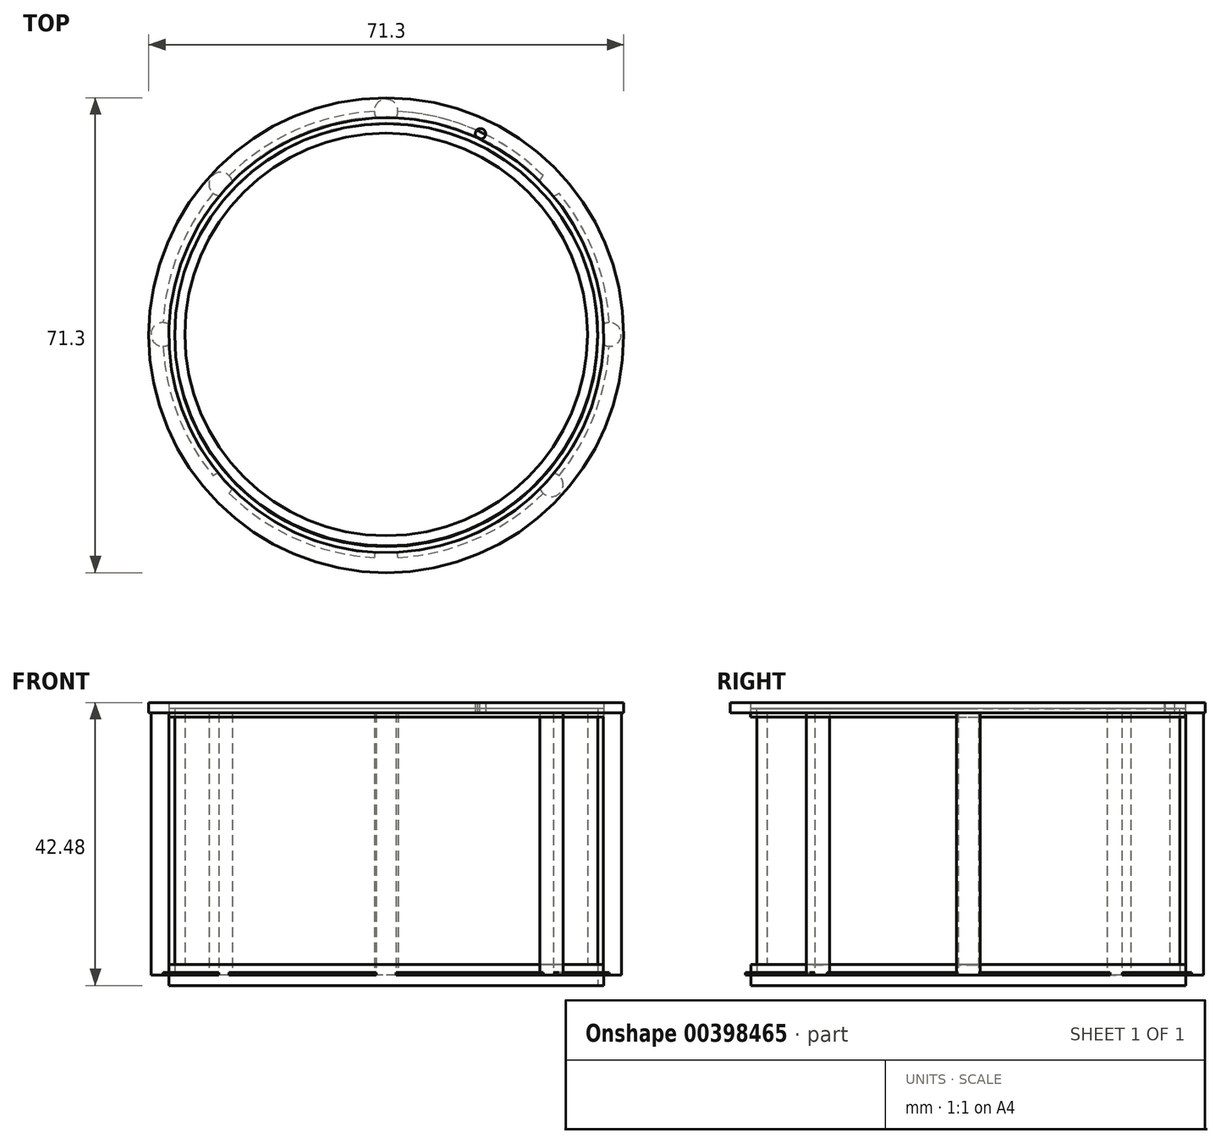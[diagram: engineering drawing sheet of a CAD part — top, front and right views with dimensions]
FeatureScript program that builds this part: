
annotation { "Feature Type Name" : "Feature", "Feature Type Description" : "" }
export const myFeature = defineFeature(function(context is Context, id is Id, definition is map)
    precondition{}
    {
        {
            var Q0;
            Q0=qCreatedBy(makeId("Top.planeOp"),FACE);
            var sketch = newSketch(context, id + "F0", { "sketchPlane" : qUnion([Q0])});
            skCircle(sketch, "E0", {"center": v(0, 0) * mm, "radius": 31.75 * mm});
            skCircle(sketch, "E1.0", {"center": v(0, 0) * mm, "radius": 32.64 * mm});
            skArc(sketch, "E2.0", {"start": v(-1.78, 33.48) * mm, "mid": v(-13.56, 30.67) * mm, "end": v(-23.57, 23.85) * mm});
            skArc(sketch, "E3.trimOffspring", {"start": v(1.78, 33.48) * mm, "mid": v(0, 35.3) * mm, "end": v(-1.78, 33.48) * mm});
            skArc(sketch, "E4.trimOffspring", {"start": v(1.78, -33.48) * mm, "mid": v(13.56, -30.67) * mm, "end": v(23.57, -23.85) * mm});
            skArc(sketch, "E5.trimOffspring", {"start": v(1.78, -33.48) * mm, "mid": v(0, -35.3) * mm, "end": v(-1.78, -33.48) * mm});
            skArc(sketch, "E6", {"start": v(-33.48, 1.78) * mm, "mid": v(-35.3, 0) * mm, "end": v(-33.48, -1.78) * mm});
            skArc(sketch, "E7", {"start": v(33.48, -1.78) * mm, "mid": v(35.3, 0) * mm, "end": v(33.48, 1.78) * mm});
            skArc(sketch, "E8.MirrorC", {"start": v(-23.57, -23.85) * mm, "mid": v(-26.11, -23.76) * mm, "end": v(-25.96, -21.22) * mm});
            skArc(sketch, "E9.MirrorC", {"start": v(23.57, -23.85) * mm, "mid": v(26.11, -23.76) * mm, "end": v(25.96, -21.22) * mm});
            skArc(sketch, "E10.MirrorC", {"start": v(23.57, 23.85) * mm, "mid": v(26.11, 23.76) * mm, "end": v(25.96, 21.22) * mm});
            skLineSegment(sketch, "E11", {"start": v(12.03, 31.3) * mm, "end": v(12.79, 33.23) * mm});
            skLineSegment(sketch, "E12", {"start": v(12.79, 33.23) * mm, "end": v(14.96, 32.39) * mm});
            skLineSegment(sketch, "E13", {"start": v(14.96, 32.39) * mm, "end": v(14.18, 30.38) * mm});
            skCircle(sketch, "E14", {"center": v(13.5, 31.8) * mm, "radius": 0.78 * mm});
            skPoint(sketch, "E14.first.point", {"position": v(13.63, 32.56) * mm});
            skPoint(sketch, "E14.second.point", {"position": v(13.3, 31.04) * mm});
            skPoint(sketch, "E14.third.point", {"position": v(13.64, 31.03) * mm});
            skArc(sketch, "E15.trimOffspring", {"start": v(25.96, -21.22) * mm, "mid": v(31.27, -12.1) * mm, "end": v(33.48, -1.78) * mm});
            skArc(sketch, "E16.trimOffspring", {"start": v(-23.57, -23.85) * mm, "mid": v(-13.56, -30.67) * mm, "end": v(-1.78, -33.48) * mm});
            skArc(sketch, "E17.trimOffspring", {"start": v(-33.48, -1.78) * mm, "mid": v(-31.27, -12.1) * mm, "end": v(-25.96, -21.22) * mm});
            skArc(sketch, "E18.trimOffspring", {"start": v(33.48, 1.78) * mm, "mid": v(31.27, 12.1) * mm, "end": v(25.96, 21.22) * mm});
            skArc(sketch, "E19.trimOffspring", {"start": v(23.57, 23.85) * mm, "mid": v(13.56, 30.67) * mm, "end": v(1.78, 33.48) * mm});
            skArc(sketch, "E20.trimOffspring", {"start": v(-25.96, 21.22) * mm, "mid": v(-31.27, 12.1) * mm, "end": v(-33.48, 1.78) * mm});
            skArc(sketch, "E21", {"start": v(25.96, -21.22) * mm, "mid": v(23.48, -21.37) * mm, "end": v(23.57, -23.85) * mm});
            skArc(sketch, "E22", {"start": v(33.48, 1.78) * mm, "mid": v(31.75, 0) * mm, "end": v(33.48, -1.78) * mm});
            skArc(sketch, "E23", {"start": v(1.78, 33.48) * mm, "mid": v(0, 31.75) * mm, "end": v(-1.78, 33.48) * mm});
            skArc(sketch, "E24", {"start": v(23.57, 23.85) * mm, "mid": v(23.48, 21.37) * mm, "end": v(25.96, 21.22) * mm});
            skArc(sketch, "E25", {"start": v(-33.48, 1.78) * mm, "mid": v(-31.75, 0) * mm, "end": v(-33.48, -1.78) * mm});
            skArc(sketch, "E26", {"start": v(-25.96, -21.22) * mm, "mid": v(-23.48, -21.37) * mm, "end": v(-23.57, -23.85) * mm});
            skArc(sketch, "E27", {"start": v(1.78, -33.48) * mm, "mid": v(0, -31.75) * mm, "end": v(-1.78, -33.48) * mm});
            skCircle(sketch, "E28", {"center": v(-24.82, 22.59) * mm, "radius": 1.78 * mm});
            skPoint(sketch, "E28.third.point", {"position": v(-26.55, 22.18) * mm});
            skSolve(sketch);
        }
        {
            var Q0;
            Q0=makeQuery(id+"F0.imprint","IMPRINT",FACE,{"disambiguationData":[TD([[makeQuery(id+"F0.imprint","IMPRINT",EDGE,{"derivedFrom":sQuery(id+"F0.wireOp",EDGE,"E0")}),1.0]])]});
            var Q1;
            {var subQ4=sQuery(id+"F0.wireOp",EDGE,"E7");Q1=makeQuery(id+"F0.imprint","IMPRINT",FACE,{"disambiguationData":[TD([[makeQuery(id+"F0.imprint","IMPRINT",EDGE,{"derivedFrom":subQ4}),1.0]])]});}
            var Q2;
            {var subQ4=sQuery(id+"F0.wireOp",EDGE,"E9.MirrorC");Q2=makeQuery(id+"F0.imprint","IMPRINT",FACE,{"disambiguationData":[TD([[makeQuery(id+"F0.imprint","IMPRINT",EDGE,{"derivedFrom":subQ4}),1.0]])]});}
            var Q3;
            Q3=makeQuery(id+"F0.imprint","IMPRINT",FACE,{"disambiguationData":[TD([[makeQuery(id+"F0.imprint","IMPRINT",EDGE,{"derivedFrom":sQuery(id+"F0.wireOp",EDGE,"E5.trimOffspring")}),-1.0]])]});
            var Q4;
            Q4=makeQuery(id+"F0.imprint","IMPRINT",FACE,{"disambiguationData":[TD([[makeQuery(id+"F0.imprint","IMPRINT",EDGE,{"derivedFrom":sQuery(id+"F0.wireOp",EDGE,"E8.MirrorC")}),-1.0]])]});
            var Q5;
            Q5=makeQuery(id+"F0.imprint","IMPRINT",FACE,{"disambiguationData":[TD([[makeQuery(id+"F0.imprint","IMPRINT",EDGE,{"derivedFrom":sQuery(id+"F0.wireOp",EDGE,"E10.MirrorC")}),-1.0]])]});
            var Q6;
            Q6=makeQuery(id+"F0.imprint","IMPRINT",FACE,{"disambiguationData":[TD([[makeQuery(id+"F0.imprint","IMPRINT",EDGE,{"derivedFrom":sQuery(id+"F0.wireOp",EDGE,"E3.trimOffspring")}),1.0]])]});
            var Q7;
            Q7=makeQuery(id+"F0.imprint","IMPRINT",FACE,{"disambiguationData":[TD([[makeQuery(id+"F0.imprint","IMPRINT",EDGE,{"derivedFrom":sQuery(id+"F0.wireOp",EDGE,"882b732f-c852-48f1-b691-361df414e5d00.MirrorC")}),1.0]])]});
            var Q8;
            {var subQ0=sQuery(id+"F0.wireOp",EDGE,"E28");var subQ1=sQuery(id+"F0.wireOp",EDGE,"E1.0");var subQ2=makeQuery(id+"F0.imprint","INTERSECT",VERTEX,{"disambiguationData":[OD(0.0)],"derivedFrom":[subQ1,subQ0]});Q8=makeQuery(id+"F0.imprint","IMPRINT",FACE,{"disambiguationData":[TD([[makeQuery(id+"F0.imprint","IMPRINT",EDGE,{"disambiguationData":[TD([[subQ2,-1.0]])],"derivedFrom":subQ1}),-1.0]])]});}
            var Q9;
            {var subQ4=sQuery(id+"F0.wireOp",EDGE,"E6");Q9=makeQuery(id+"F0.imprint","IMPRINT",FACE,{"disambiguationData":[TD([[makeQuery(id+"F0.imprint","IMPRINT",EDGE,{"derivedFrom":subQ4}),1.0]])]});}
            extrude(context, id + "F1", {"entities" : qUnion([Q0, Q1, Q2, Q3, Q4, Q5, Q6, Q7, Q8, Q9]), "depth" : 39.37 * mm});
        }
        {
            var Q0;
            {var subQ0=sQuery(id+"F0.wireOp",EDGE,"E23");var subQ1=sQuery(id+"F0.wireOp",EDGE,"E0");var subQ2=makeQuery(id+"F0.imprint","INTERSECT",VERTEX,{"derivedFrom":[subQ1,subQ0]});Q0=makeQuery(id+"F0.imprint","IMPRINT",FACE,{"disambiguationData":[TD([[makeQuery(id+"F0.imprint","IMPRINT",EDGE,{"disambiguationData":[TD([[subQ2,-1.0]])],"derivedFrom":subQ1}),-1.0]])]});}
            var Q1;
            {var subQ0=sQuery(id+"F0.wireOp",EDGE,"E28");var subQ1=sQuery(id+"F0.wireOp",EDGE,"E1.0");var subQ2=makeQuery(id+"F0.imprint","INTERSECT",VERTEX,{"disambiguationData":[OD(0.0)],"derivedFrom":[subQ1,subQ0]});Q1=makeQuery(id+"F0.imprint","IMPRINT",FACE,{"disambiguationData":[TD([[makeQuery(id+"F0.imprint","IMPRINT",EDGE,{"disambiguationData":[TD([[subQ2,-1.0]])],"derivedFrom":subQ1}),1.0]])]});}
            var Q2;
            {var subQ0=sQuery(id+"F0.wireOp",EDGE,"E24");var subQ1=sQuery(id+"F0.wireOp",EDGE,"E0");var subQ2=makeQuery(id+"F0.imprint","INTERSECT",VERTEX,{"derivedFrom":[subQ1,subQ0]});Q2=makeQuery(id+"F0.imprint","IMPRINT",FACE,{"disambiguationData":[TD([[makeQuery(id+"F0.imprint","IMPRINT",EDGE,{"disambiguationData":[TD([[subQ2,-1.0]])],"derivedFrom":subQ1}),-1.0]])]});}
            var Q3;
            {var subQ0=sQuery(id+"F0.wireOp",EDGE,"E23");var subQ1=sQuery(id+"F0.wireOp",EDGE,"E1.0");var subQ2=makeQuery(id+"F0.imprint","INTERSECT",VERTEX,{"disambiguationData":[OD(0.0)],"derivedFrom":[subQ1,subQ0]});Q3=makeQuery(id+"F0.imprint","IMPRINT",FACE,{"disambiguationData":[TD([[makeQuery(id+"F0.imprint","IMPRINT",EDGE,{"disambiguationData":[TD([[subQ2,-1.0]])],"derivedFrom":subQ1}),1.0]])]});}
            var Q4;
            {var subQ0=sQuery(id+"F0.wireOp",EDGE,"E24");var subQ1=sQuery(id+"F0.wireOp",EDGE,"E1.0");var subQ2=makeQuery(id+"F0.imprint","INTERSECT",VERTEX,{"disambiguationData":[OD(0.0)],"derivedFrom":[subQ1,subQ0]});Q4=makeQuery(id+"F0.imprint","IMPRINT",FACE,{"disambiguationData":[TD([[makeQuery(id+"F0.imprint","IMPRINT",EDGE,{"disambiguationData":[TD([[subQ2,-1.0]])],"derivedFrom":subQ1}),1.0]])]});}
            var Q5;
            {var subQ0=sQuery(id+"F0.wireOp",EDGE,"E24");var subQ1=sQuery(id+"F0.wireOp",EDGE,"E0");var subQ2=makeQuery(id+"F0.imprint","INTERSECT",VERTEX,{"derivedFrom":[subQ1,subQ0]});Q5=makeQuery(id+"F0.imprint","IMPRINT",FACE,{"disambiguationData":[TD([[makeQuery(id+"F0.imprint","IMPRINT",EDGE,{"disambiguationData":[TD([[subQ2,1.0]])],"derivedFrom":subQ1}),-1.0]])]});}
            var Q6;
            {var subQ0=sQuery(id+"F0.wireOp",EDGE,"E22");var subQ1=sQuery(id+"F0.wireOp",EDGE,"E1.0");var subQ2=makeQuery(id+"F0.imprint","INTERSECT",VERTEX,{"disambiguationData":[OD(0.0)],"derivedFrom":[subQ1,subQ0]});Q6=makeQuery(id+"F0.imprint","IMPRINT",FACE,{"disambiguationData":[TD([[makeQuery(id+"F0.imprint","IMPRINT",EDGE,{"disambiguationData":[TD([[subQ2,1.0]])],"derivedFrom":subQ1}),1.0]])]});}
            var Q7;
            {var subQ0=sQuery(id+"F0.wireOp",EDGE,"E22");var subQ1=sQuery(id+"F0.wireOp",EDGE,"E0");var subQ2=makeQuery(id+"F0.imprint","INTERSECT",VERTEX,{"derivedFrom":[subQ1,subQ0]});Q7=makeQuery(id+"F0.imprint","IMPRINT",FACE,{"disambiguationData":[TD([[makeQuery(id+"F0.imprint","IMPRINT",EDGE,{"disambiguationData":[TD([[subQ2,1.0]])],"derivedFrom":subQ1}),-1.0]])]});}
            var Q8;
            {var subQ0=sQuery(id+"F0.wireOp",EDGE,"E21");var subQ1=sQuery(id+"F0.wireOp",EDGE,"E1.0");var subQ2=makeQuery(id+"F0.imprint","INTERSECT",VERTEX,{"disambiguationData":[OD(0.0)],"derivedFrom":[subQ1,subQ0]});Q8=makeQuery(id+"F0.imprint","IMPRINT",FACE,{"disambiguationData":[TD([[makeQuery(id+"F0.imprint","IMPRINT",EDGE,{"disambiguationData":[TD([[subQ2,-1.0]])],"derivedFrom":subQ1}),1.0]])]});}
            var Q9;
            {var subQ0=sQuery(id+"F0.wireOp",EDGE,"E27");var subQ1=sQuery(id+"F0.wireOp",EDGE,"E0");var subQ2=makeQuery(id+"F0.imprint","INTERSECT",VERTEX,{"derivedFrom":[subQ1,subQ0]});Q9=makeQuery(id+"F0.imprint","IMPRINT",FACE,{"disambiguationData":[TD([[makeQuery(id+"F0.imprint","IMPRINT",EDGE,{"disambiguationData":[TD([[subQ2,-1.0]])],"derivedFrom":subQ1}),-1.0]])]});}
            var Q10;
            {var subQ0=sQuery(id+"F0.wireOp",EDGE,"E27");var subQ1=sQuery(id+"F0.wireOp",EDGE,"E1.0");var subQ2=makeQuery(id+"F0.imprint","INTERSECT",VERTEX,{"disambiguationData":[OD(0.0)],"derivedFrom":[subQ1,subQ0]});Q10=makeQuery(id+"F0.imprint","IMPRINT",FACE,{"disambiguationData":[TD([[makeQuery(id+"F0.imprint","IMPRINT",EDGE,{"disambiguationData":[TD([[subQ2,-1.0]])],"derivedFrom":subQ1}),1.0]])]});}
            var Q11;
            {var subQ0=sQuery(id+"F0.wireOp",EDGE,"E26");var subQ1=sQuery(id+"F0.wireOp",EDGE,"E0");var subQ2=makeQuery(id+"F0.imprint","INTERSECT",VERTEX,{"derivedFrom":[subQ1,subQ0]});Q11=makeQuery(id+"F0.imprint","IMPRINT",FACE,{"disambiguationData":[TD([[makeQuery(id+"F0.imprint","IMPRINT",EDGE,{"disambiguationData":[TD([[subQ2,-1.0]])],"derivedFrom":subQ1}),-1.0]])]});}
            var Q12;
            {var subQ0=sQuery(id+"F0.wireOp",EDGE,"E26");var subQ1=sQuery(id+"F0.wireOp",EDGE,"E1.0");var subQ2=makeQuery(id+"F0.imprint","INTERSECT",VERTEX,{"disambiguationData":[OD(0.0)],"derivedFrom":[subQ1,subQ0]});Q12=makeQuery(id+"F0.imprint","IMPRINT",FACE,{"disambiguationData":[TD([[makeQuery(id+"F0.imprint","IMPRINT",EDGE,{"disambiguationData":[TD([[subQ2,-1.0]])],"derivedFrom":subQ1}),1.0]])]});}
            var Q13;
            {var subQ0=sQuery(id+"F0.wireOp",EDGE,"E25");var subQ1=sQuery(id+"F0.wireOp",EDGE,"E0");var subQ2=makeQuery(id+"F0.imprint","INTERSECT",VERTEX,{"derivedFrom":[subQ1,subQ0]});Q13=makeQuery(id+"F0.imprint","IMPRINT",FACE,{"disambiguationData":[TD([[makeQuery(id+"F0.imprint","IMPRINT",EDGE,{"disambiguationData":[TD([[subQ2,-1.0]])],"derivedFrom":subQ1}),-1.0]])]});}
            var Q14;
            {var subQ0=sQuery(id+"F0.wireOp",EDGE,"E25");var subQ1=sQuery(id+"F0.wireOp",EDGE,"E1.0");var subQ2=makeQuery(id+"F0.imprint","INTERSECT",VERTEX,{"disambiguationData":[OD(0.0)],"derivedFrom":[subQ1,subQ0]});Q14=makeQuery(id+"F0.imprint","IMPRINT",FACE,{"disambiguationData":[TD([[makeQuery(id+"F0.imprint","IMPRINT",EDGE,{"disambiguationData":[TD([[subQ2,-1.0]])],"derivedFrom":subQ1}),1.0]])]});}
            extrude(context, id + "F2", {"entities" : qUnion([Q0, Q1, Q2, Q3, Q4, Q5, Q6, Q7, Q8, Q9, Q10, Q11, Q12, Q13, Q14]), "endBound" : BoundingType.SYMMETRIC, "depth" : 3.17 * mm});
        }
        {
            var Q0;
            {var subQ5=sQuery(id+"F0.wireOp",EDGE,"E2.0");Q0=makeQuery(id+"F0.imprint","IMPRINT",FACE,{"disambiguationData":[TD([[makeQuery(id+"F0.imprint","IMPRINT",EDGE,{"derivedFrom":subQ5}),1.0]])]});}
            var Q1;
            {var subQ4=sQuery(id+"F0.wireOp",EDGE,"E24");var subQ5=sQuery(id+"F0.wireOp",EDGE,"E1.0");var subQ6=makeQuery(id+"F0.imprint","INTERSECT",VERTEX,{"disambiguationData":[OD(1.0)],"derivedFrom":[subQ5,subQ4]});Q1=makeQuery(id+"F0.imprint","IMPRINT",FACE,{"disambiguationData":[TD([[makeQuery(id+"F0.imprint","IMPRINT",EDGE,{"disambiguationData":[TD([[subQ6,-1.0]])],"derivedFrom":subQ5}),-1.0]])]});}
            var Q2;
            {var subQ5=sQuery(id+"F0.wireOp",EDGE,"E18.trimOffspring");Q2=makeQuery(id+"F0.imprint","IMPRINT",FACE,{"disambiguationData":[TD([[makeQuery(id+"F0.imprint","IMPRINT",EDGE,{"derivedFrom":subQ5}),1.0]])]});}
            var Q3;
            {var subQ5=sQuery(id+"F0.wireOp",EDGE,"E15.trimOffspring");Q3=makeQuery(id+"F0.imprint","IMPRINT",FACE,{"disambiguationData":[TD([[makeQuery(id+"F0.imprint","IMPRINT",EDGE,{"derivedFrom":subQ5}),1.0]])]});}
            var Q4;
            {var subQ5=sQuery(id+"F0.wireOp",EDGE,"E4.trimOffspring");Q4=makeQuery(id+"F0.imprint","IMPRINT",FACE,{"disambiguationData":[TD([[makeQuery(id+"F0.imprint","IMPRINT",EDGE,{"derivedFrom":subQ5}),1.0]])]});}
            var Q5;
            {var subQ5=sQuery(id+"F0.wireOp",EDGE,"E16.trimOffspring");Q5=makeQuery(id+"F0.imprint","IMPRINT",FACE,{"disambiguationData":[TD([[makeQuery(id+"F0.imprint","IMPRINT",EDGE,{"derivedFrom":subQ5}),1.0]])]});}
            var Q6;
            {var subQ5=sQuery(id+"F0.wireOp",EDGE,"E17.trimOffspring");Q6=makeQuery(id+"F0.imprint","IMPRINT",FACE,{"disambiguationData":[TD([[makeQuery(id+"F0.imprint","IMPRINT",EDGE,{"derivedFrom":subQ5}),1.0]])]});}
            var Q7;
            {var subQ5=sQuery(id+"F0.wireOp",EDGE,"E20.trimOffspring");Q7=makeQuery(id+"F0.imprint","IMPRINT",FACE,{"disambiguationData":[TD([[makeQuery(id+"F0.imprint","IMPRINT",EDGE,{"derivedFrom":subQ5}),1.0]])]});}
            extrude(context, id + "F3", {"entities" : qUnion([Q0, Q1, Q2, Q3, Q4, Q5, Q6, Q7]), "depth" : 0.38 * mm});
        }
        {
            var Q0;
            Q0=makeQuery(id+"F1.opExtrude","CAP_FACE",FACE,{"disambiguationData":[OSD([sQuery(id+"F0.wireOp",EDGE,"E0")])],"isStart":false});
            var sketch = newSketch(context, id + "F4", { "sketchPlane" : qUnion([Q0])});
            skCircle(sketch, "E29", {"center": v(0.02, -0.11) * mm, "radius": 31.75 * mm});
            skCircle(sketch, "E30.0", {"center": v(0.02, -0.11) * mm, "radius": 32.64 * mm});
            skPoint(sketch, "E31.center.orphan", {"position": v(0.7, 33.4) * mm});
            skLineSegment(sketch, "E32", {"start": v(13.14, 30.74) * mm, "end": v(13.46, 31.58) * mm});
            skLineSegment(sketch, "E33", {"start": v(13.46, 31.58) * mm, "end": v(15.63, 30.73) * mm});
            skLineSegment(sketch, "E34", {"start": v(15.63, 30.73) * mm, "end": v(15.25, 29.76) * mm});
            skCircle(sketch, "E35", {"center": v(14.17, 30.14) * mm, "radius": 0.78 * mm});
            skPoint(sketch, "E35.first.point", {"position": v(14.3, 30.9) * mm});
            skPoint(sketch, "E35.second.point", {"position": v(13.97, 29.39) * mm});
            skPoint(sketch, "E35.third.point", {"position": v(14.31, 29.37) * mm});
            skPoint(sketch, "E36.third.point", {"position": v(-25.88, 20.53) * mm});
            skCircle(sketch, "E37.0", {"center": v(0.02, -0.11) * mm, "radius": 35.65 * mm});
            skSolve(sketch);
        }
        {
            var Q0;
            {var subQ0=sQuery(id+"F4.wireOp",EDGE,"05f0027a-2171-4007-9836-8562fc80002a");var subQ1=sQuery(id+"F4.wireOp",EDGE,"E29");var subQ2=makeQuery(id+"F4.imprint","INTERSECT",VERTEX,{"disambiguationData":[OD(0.0)],"derivedFrom":[subQ1,subQ0]});Q0=makeQuery(id+"F4.imprint","IMPRINT",FACE,{"disambiguationData":[TD([[makeQuery(id+"F4.imprint","IMPRINT",EDGE,{"disambiguationData":[TD([[subQ2,-1.0]])],"derivedFrom":subQ1}),-1.0]])]});}
            var Q1;
            {var subQ0=sQuery(id+"F4.wireOp",EDGE,"05f0027a-2171-4007-9836-8562fc80002a");var subQ1=sQuery(id+"F4.wireOp",EDGE,"E29");var subQ2=makeQuery(id+"F4.imprint","INTERSECT",VERTEX,{"disambiguationData":[OD(1.0)],"derivedFrom":[subQ1,subQ0]});Q1=makeQuery(id+"F4.imprint","IMPRINT",FACE,{"disambiguationData":[TD([[makeQuery(id+"F4.imprint","IMPRINT",EDGE,{"disambiguationData":[TD([[subQ2,-1.0]])],"derivedFrom":subQ1}),-1.0]])]});}
            var Q2;
            {var subQ0=sQuery(id+"F4.wireOp",EDGE,"f87926d4-d22f-4db6-bb2e-eca88a423e5e");var subQ1=sQuery(id+"F4.wireOp",EDGE,"E29");var subQ2=makeQuery(id+"F4.imprint","INTERSECT",VERTEX,{"disambiguationData":[OD(1.0)],"derivedFrom":[subQ1,subQ0]});Q2=makeQuery(id+"F4.imprint","IMPRINT",FACE,{"disambiguationData":[TD([[makeQuery(id+"F4.imprint","IMPRINT",EDGE,{"disambiguationData":[TD([[subQ2,-1.0]])],"derivedFrom":subQ1}),-1.0]])]});}
            var Q3;
            {var subQ0=sQuery(id+"F4.wireOp",EDGE,"f87926d4-d22f-4db6-bb2e-eca88a423e5e");var subQ1=sQuery(id+"F4.wireOp",EDGE,"E29");var subQ2=makeQuery(id+"F4.imprint","INTERSECT",VERTEX,{"disambiguationData":[OD(0.0)],"derivedFrom":[subQ1,subQ0]});Q3=makeQuery(id+"F4.imprint","IMPRINT",FACE,{"disambiguationData":[TD([[makeQuery(id+"F4.imprint","IMPRINT",EDGE,{"disambiguationData":[TD([[subQ2,-1.0]])],"derivedFrom":subQ1}),-1.0]])]});}
            var Q4;
            {var subQ0=sQuery(id+"F4.wireOp",EDGE,"77c8a3e9-4459-4353-a445-deef52aa50ce");var subQ1=sQuery(id+"F4.wireOp",EDGE,"E29");var subQ2=makeQuery(id+"F4.imprint","INTERSECT",VERTEX,{"disambiguationData":[OD(1.0)],"derivedFrom":[subQ1,subQ0]});Q4=makeQuery(id+"F4.imprint","IMPRINT",FACE,{"disambiguationData":[TD([[makeQuery(id+"F4.imprint","IMPRINT",EDGE,{"disambiguationData":[TD([[subQ2,-1.0]])],"derivedFrom":subQ1}),-1.0]])]});}
            var Q5;
            {var subQ0=sQuery(id+"F4.wireOp",EDGE,"77c8a3e9-4459-4353-a445-deef52aa50ce");var subQ1=sQuery(id+"F4.wireOp",EDGE,"E29");var subQ2=makeQuery(id+"F4.imprint","INTERSECT",VERTEX,{"disambiguationData":[OD(0.0)],"derivedFrom":[subQ1,subQ0]});Q5=makeQuery(id+"F4.imprint","IMPRINT",FACE,{"disambiguationData":[TD([[makeQuery(id+"F4.imprint","IMPRINT",EDGE,{"disambiguationData":[TD([[subQ2,-1.0]])],"derivedFrom":subQ1}),-1.0]])]});}
            var Q6;
            {var subQ0=sQuery(id+"F4.wireOp",EDGE,"77c8a3e9-4459-4353-a445-deef52aa50ce");var subQ1=sQuery(id+"F4.wireOp",EDGE,"E29");var subQ2=makeQuery(id+"F4.imprint","INTERSECT",VERTEX,{"disambiguationData":[OD(0.0)],"derivedFrom":[subQ1,subQ0]});Q6=makeQuery(id+"F4.imprint","IMPRINT",FACE,{"disambiguationData":[TD([[makeQuery(id+"F4.imprint","IMPRINT",EDGE,{"disambiguationData":[TD([[subQ2,1.0]])],"derivedFrom":subQ1}),-1.0]])]});}
            var Q7;
            {var subQ0=sQuery(id+"F4.wireOp",EDGE,"E36");var subQ1=sQuery(id+"F4.wireOp",EDGE,"E30.0");var subQ2=makeQuery(id+"F4.imprint","INTERSECT",VERTEX,{"disambiguationData":[OD(1.0)],"derivedFrom":[subQ1,subQ0]});Q7=makeQuery(id+"F4.imprint","IMPRINT",FACE,{"disambiguationData":[TD([[makeQuery(id+"F4.imprint","IMPRINT",EDGE,{"disambiguationData":[TD([[subQ2,-1.0]])],"derivedFrom":subQ1}),1.0]])]});}
            var Q8;
            {var subQ0=sQuery(id+"F4.wireOp",EDGE,"c04478a5-35ab-4bfc-905c-95152bf91cf8");var subQ1=sQuery(id+"F4.wireOp",EDGE,"E30.0");var subQ2=makeQuery(id+"F4.imprint","INTERSECT",VERTEX,{"disambiguationData":[OD(0.0)],"derivedFrom":[subQ1,subQ0]});Q8=makeQuery(id+"F4.imprint","IMPRINT",FACE,{"disambiguationData":[TD([[makeQuery(id+"F4.imprint","IMPRINT",EDGE,{"disambiguationData":[TD([[subQ2,-1.0]])],"derivedFrom":subQ1}),1.0]])]});}
            var Q9;
            {var subQ0=sQuery(id+"F4.wireOp",EDGE,"E36");var subQ1=sQuery(id+"F4.wireOp",EDGE,"E30.0");var subQ2=makeQuery(id+"F4.imprint","INTERSECT",VERTEX,{"disambiguationData":[OD(0.0)],"derivedFrom":[subQ1,subQ0]});Q9=makeQuery(id+"F4.imprint","IMPRINT",FACE,{"disambiguationData":[TD([[makeQuery(id+"F4.imprint","IMPRINT",EDGE,{"disambiguationData":[TD([[subQ2,-1.0]])],"derivedFrom":subQ1}),1.0]])]});}
            var Q10;
            {var subQ0=sQuery(id+"F4.wireOp",EDGE,"269bba93-a568-4ed9-8eb2-4e7f6a127117");var subQ1=sQuery(id+"F4.wireOp",EDGE,"E30.0");var subQ2=makeQuery(id+"F4.imprint","INTERSECT",VERTEX,{"disambiguationData":[OD(1.0)],"derivedFrom":[subQ1,subQ0]});Q10=makeQuery(id+"F4.imprint","IMPRINT",FACE,{"disambiguationData":[TD([[makeQuery(id+"F4.imprint","IMPRINT",EDGE,{"disambiguationData":[TD([[subQ2,-1.0]])],"derivedFrom":subQ1}),1.0]])]});}
            var Q11;
            {var subQ0=sQuery(id+"F4.wireOp",EDGE,"269bba93-a568-4ed9-8eb2-4e7f6a127117");var subQ1=sQuery(id+"F4.wireOp",EDGE,"E30.0");var subQ2=makeQuery(id+"F4.imprint","INTERSECT",VERTEX,{"disambiguationData":[OD(0.0)],"derivedFrom":[subQ1,subQ0]});Q11=makeQuery(id+"F4.imprint","IMPRINT",FACE,{"disambiguationData":[TD([[makeQuery(id+"F4.imprint","IMPRINT",EDGE,{"disambiguationData":[TD([[subQ2,-1.0]])],"derivedFrom":subQ1}),1.0]])]});}
            var Q12;
            {var subQ1=sQuery(id+"F4.wireOp",EDGE,"E30.0");var subQ8=sQuery(id+"F4.wireOp",EDGE,"8928fb85-3d40-493b-ba61-79e21443b8ce");var subQ9=makeQuery(id+"F4.imprint","INTERSECT",VERTEX,{"disambiguationData":[OD(1.0)],"derivedFrom":[subQ1,subQ8]});Q12=makeQuery(id+"F4.imprint","IMPRINT",FACE,{"disambiguationData":[TD([[makeQuery(id+"F4.imprint","IMPRINT",EDGE,{"disambiguationData":[TD([[subQ9,-1.0]])],"derivedFrom":subQ1}),1.0]])]});}
            var Q13;
            {var subQ0=sQuery(id+"F4.wireOp",EDGE,"8928fb85-3d40-493b-ba61-79e21443b8ce");var subQ1=sQuery(id+"F4.wireOp",EDGE,"E30.0");var subQ2=makeQuery(id+"F4.imprint","INTERSECT",VERTEX,{"disambiguationData":[OD(0.0)],"derivedFrom":[subQ1,subQ0]});Q13=makeQuery(id+"F4.imprint","IMPRINT",FACE,{"disambiguationData":[TD([[makeQuery(id+"F4.imprint","IMPRINT",EDGE,{"disambiguationData":[TD([[subQ2,-1.0]])],"derivedFrom":subQ1}),1.0]])]});}
            var Q14;
            {var subQ5=sQuery(id+"F4.wireOp",EDGE,"09ed5a69-8966-462d-8de5-d18fd240edf1");var subQ6=sQuery(id+"F4.wireOp",EDGE,"E29");var subQ7=makeQuery(id+"F4.imprint","INTERSECT",VERTEX,{"derivedFrom":[subQ6,subQ5]});Q14=makeQuery(id+"F4.imprint","IMPRINT",FACE,{"disambiguationData":[TD([[makeQuery(id+"F4.imprint","IMPRINT",EDGE,{"disambiguationData":[TD([[subQ7,-1.0]])],"derivedFrom":subQ6}),-1.0]])]});}
            var Q15;
            {var subQ0=sQuery(id+"F4.wireOp",EDGE,"09ed5a69-8966-462d-8de5-d18fd240edf1");var subQ1=sQuery(id+"F4.wireOp",EDGE,"E30.0");var subQ2=makeQuery(id+"F4.imprint","INTERSECT",VERTEX,{"disambiguationData":[OD(0.0)],"derivedFrom":[subQ1,subQ0]});Q15=makeQuery(id+"F4.imprint","IMPRINT",FACE,{"disambiguationData":[TD([[makeQuery(id+"F4.imprint","IMPRINT",EDGE,{"disambiguationData":[TD([[subQ2,1.0]])],"derivedFrom":subQ1}),1.0]])]});}
            extrude(context, id + "F5", {"entities" : qUnion([Q0, Q1, Q2, Q3, Q4, Q5, Q6, Q7, Q8, Q9, Q10, Q11, Q12, Q13, Q14, Q15]), "endBound" : BoundingType.SYMMETRIC, "depth" : 1.27 * mm});
        }
        {
            var Q0;
            Q0=makeQuery(id+"F4.imprint","IMPRINT",FACE,{"disambiguationData":[TD([[makeQuery(id+"F4.imprint","IMPRINT",EDGE,{"derivedFrom":sQuery(id+"F4.wireOp",EDGE,"E37.0")}),1.0]])]});
            extrude(context, id + "F6", {"entities" : qUnion([Q0]), "depth" : 1.52 * mm});
        }
        {
            var Q0;
            Q0=makeQuery(id+"F1.opExtrude","CAP_FACE",FACE,{"disambiguationData":[OSD([sQuery(id+"F0.wireOp",EDGE,"E0")])],"isStart":false});
            shell(context, id + "F7", {"entities" : qUnion([Q0]), "thickness" : 1.52 * mm});
        }
    });
